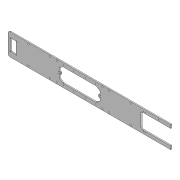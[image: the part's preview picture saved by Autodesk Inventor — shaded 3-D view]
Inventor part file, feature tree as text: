
AUTODESK INVENTOR PART (.ipt)
format: ipt  version: 2020 (Build 240168000, 168)  size: 373,248 bytes
history: native  units: mm
features: sketch x5, extrude x4, hole x4, projected_geometry x3
ambient origin geometry x8: Origin, YZ Plane, XZ Plane, XY Plane, X Axis, Y Axis, Z Axis, Center Point
bodies: Solid1 (feature_tree)
feature tree (16):
  sketch  "Sketch1"  dims[d0=400.0mm d1=3000.0mm]
  extrude  "Extrusion1"  Depth=3000.0mm
  hole  "Hole1"  [1 undecoded]
  sketch  "Sketch2"  dims[d2=30.0mm d3=110.0mm]
  extrude  "Extrusion2"  Depth=15.0mm
  hole  "Hole2"  [1 undecoded]
  sketch  "Sketch3"  dims[d4=220.0mm d5=15.0mm]
  extrude  "Extrusion3"  Depth=20.0mm
  hole  "Hole4"  [1 undecoded]
  hole  "Hole5"  [1 undecoded]
  extrude  "Extrusion4"  Depth=550.0mm
  projected_geometry  "Projected Loop1"
  sketch  "Sketch4"  dims[d8=230.0mm d9=120.0mm]
  projected_geometry  "Projected Loop2"
  sketch  "Sketch5"  dims[d10=5.0mm d11=5.0mm d12=40.0mm d13=20.0mm d14=0.0mm d15=10.106mm d16=24.0mm d17=4.0mm d18=2.0mm d19=90.0deg d20=32.3mm d21=20.594885mm d22=550.0mm d23=280.0mm d24=25.0mm d25=7.0mm d26=230.0mm d27=320.0mm d28=27.0mm d29=475.0mm d30=230.0mm d31=15.0mm d32=20.0mm d33=0.0mm d34=10.106mm d35=24.0mm d36=4.0mm d37=2.0mm d38=90.0deg d39=32.3mm d40=20.594885mm d41=756.0mm d59=20.0mm d60=0.0mm d76=262.0mm d77=35.0mm d78=15.0mm d79=32.0mm d80=189.0mm d81=9.0mm d82=20.0mm d83=1305.0mm d86=756.0mm d87=195.0mm d88=183.0mm d89=110.0mm d90=189.0mm d91=161.0mm d92=10.106mm d93=24.0mm d94=4.0mm d95=2.0mm d96=90.0deg d97=32.3mm d98=20.594885mm d99=420.0mm d100=545.0mm d101=400.0mm d102=30.0mm d103=24.0mm d104=4.0mm d105=2.0mm d106=90.0deg d107=32.3mm d108=20.594885mm d109=175.0mm d112=20.0mm d113=0.0mm]
  projected_geometry  "Projected Loop3"
note: 4 required parameter values undecoded (feature->parameter linkage not recoverable at this tier; creation-order binding heuristic only, values carry confidence <= 0.55)
